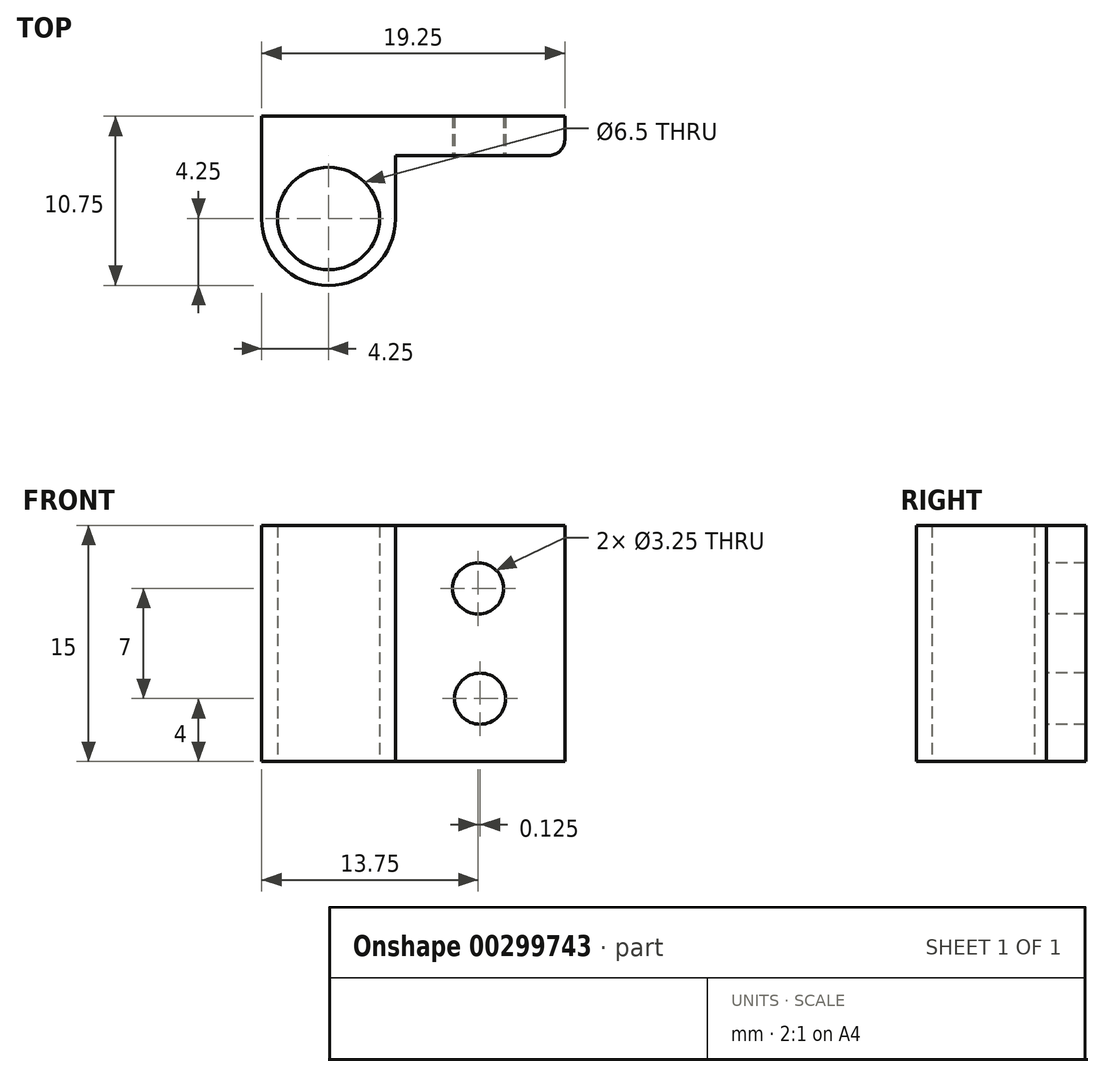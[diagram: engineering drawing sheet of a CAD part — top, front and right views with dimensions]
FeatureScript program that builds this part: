
annotation { "Feature Type Name" : "Feature", "Feature Type Description" : "" }
export const myFeature = defineFeature(function(context is Context, id is Id, definition is map)
    precondition{}
    {
        {
            var Q0;
            Q0=qCreatedBy(makeId("Top.planeOp"),FACE);
            var sketch = newSketch(context, id + "F0", { "sketchPlane" : qUnion([Q0])});
            skCircle(sketch, "E0", {"center": v(0, 0) * mm, "radius": 3.25 * mm});
            skArc(sketch, "E1", {"start": v(-4.25, 0) * mm, "mid": v(0, -4.25) * mm, "end": v(4.25, 0) * mm});
            skLineSegment(sketch, "E2", {"start": v(15, 4) * mm, "end": v(15, 6.5) * mm});
            skLineSegment(sketch, "E3", {"start": v(15, 6.5) * mm, "end": v(-4.25, 6.5) * mm});
            skLineSegment(sketch, "E4", {"start": v(-4.25, 6.5) * mm, "end": v(-4.25, 0) * mm});
            skLineSegment(sketch, "E5", {"start": v(4.25, 0) * mm, "end": v(4.25, 4) * mm});
            skLineSegment(sketch, "E6", {"start": v(15, 4) * mm, "end": v(4.25, 4) * mm});
            skSolve(sketch);
        }
        {
            var Q0;
            Q0=makeQuery(id+"F0.imprint","IMPRINT",FACE,{"disambiguationData":[TD([[makeQuery(id+"F0.imprint","IMPRINT",EDGE,{"derivedFrom":sQuery(id+"F0.wireOp",EDGE,"E0")}),-1.0]])]});
            extrude(context, id + "F1", {"entities" : qUnion([Q0]), "depth" : 15 * mm});
        }
        {
            var Q0;
            Q0=makeQuery(id+"F1.opExtrude","SWEPT_FACE",FACE,{"disambiguationData":[OSD([sQuery(id+"F0.wireOp",EDGE,"E6")])]});
            var sketch = newSketch(context, id + "F2", { "sketchPlane" : qUnion([Q0])});
            skCircle(sketch, "E7", {"center": v(9.62, 4) * mm, "radius": 1.63 * mm});
            skCircle(sketch, "E8", {"center": v(9.5, 11) * mm, "radius": 1.63 * mm});
            skSolve(sketch);
        }
        {
            var Q0;
            Q0=makeQuery(id+"F2.imprint","IMPRINT",FACE,{"disambiguationData":[TD([[makeQuery(id+"F2.imprint","IMPRINT",EDGE,{"derivedFrom":sQuery(id+"F2.wireOp",EDGE,"E8")}),1.0]])]});
            var Q1;
            Q1=makeQuery(id+"F2.imprint","IMPRINT",FACE,{"disambiguationData":[TD([[makeQuery(id+"F2.imprint","IMPRINT",EDGE,{"derivedFrom":sQuery(id+"F2.wireOp",EDGE,"E7")}),1.0]])]});
            extrude(context, id + "F3", {"entities" : qUnion([Q0, Q1]), "operationType" : NewBodyOperationType.REMOVE, "oppositeDirection" : true, "depth" : 3 * mm});
        }
        {
            var Q0;
            Q0=makeQuery(id+"F1.opExtrude","SWEPT_EDGE",EDGE,{"disambiguationData":[OSD([sQuery(id+"F0.wireOp",EDGE,"E2"),sQuery(id+"F0.wireOp",EDGE,"E6")])]});
            fillet(context, id + "F4", {"entities" : qUnion([Q0]), "radius" : 1 * mm, "tangentPropagation" : true, "allowEdgeOverflow" : false});
        }
    });
